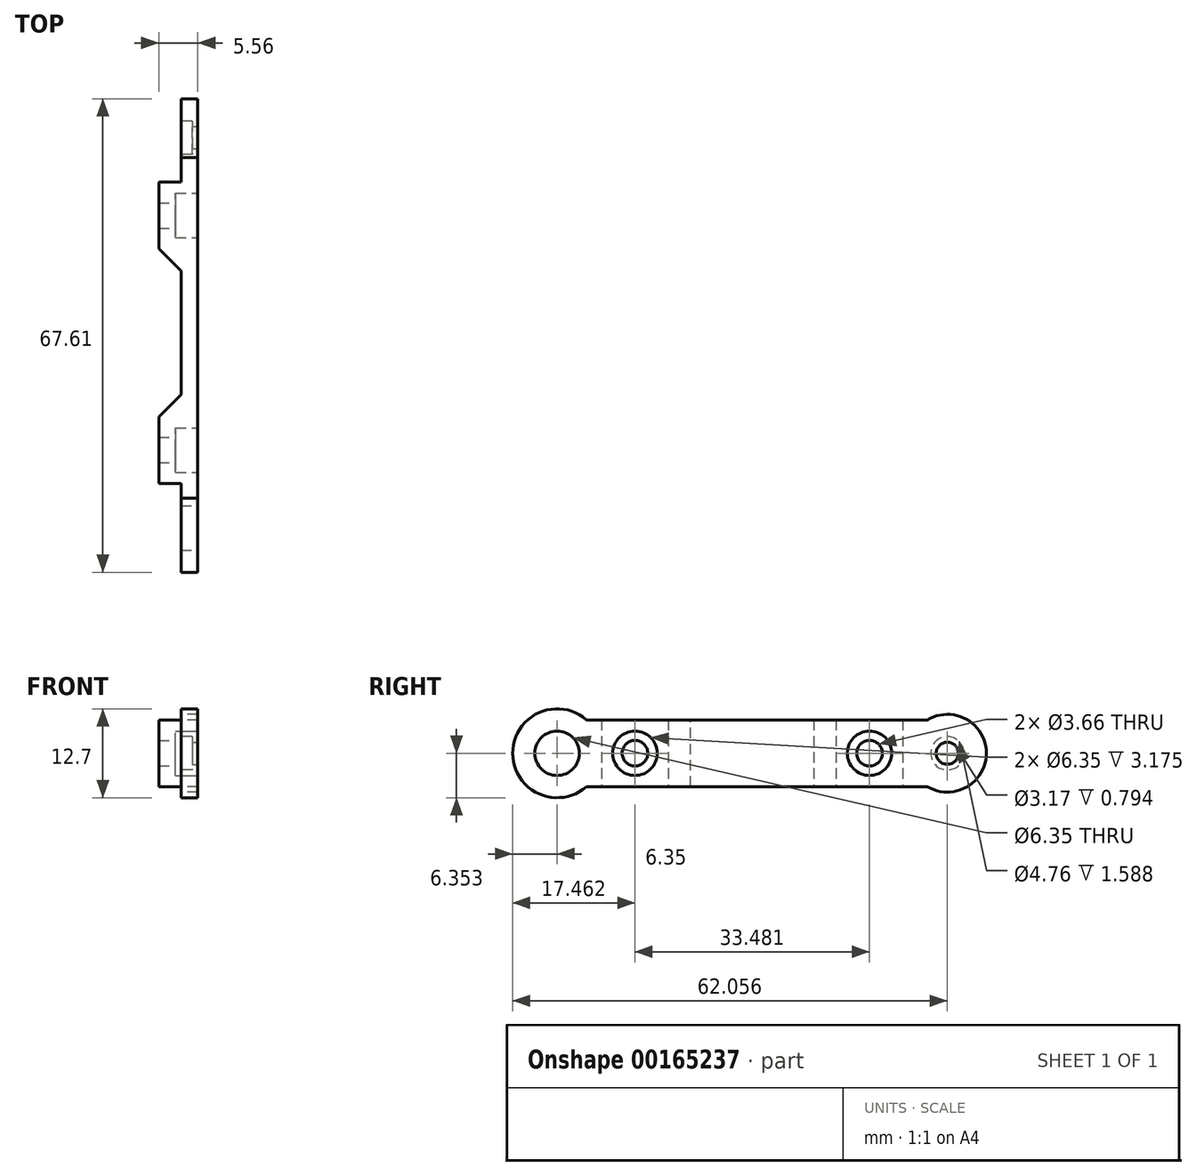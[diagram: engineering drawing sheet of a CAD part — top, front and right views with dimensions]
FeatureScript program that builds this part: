
annotation { "Feature Type Name" : "Feature", "Feature Type Description" : "" }
export const myFeature = defineFeature(function(context is Context, id is Id, definition is map)
    precondition{}
    {
        {
            var Q0;
            Q0=qCreatedBy(makeId("Top.planeOp"),FACE);
            var sketch = newSketch(context, id + "F0", { "sketchPlane" : qUnion([Q0])});
            skLineSegment(sketch, "E0.top", {"start": v(0, 55.7) * mm, "end": v(-2.38, 55.7) * mm});
            skLineSegment(sketch, "E0.left", {"start": v(0, 0) * mm, "end": v(0, 55.7) * mm});
            skLineSegment(sketch, "E0.right", {"start": v(-2.38, 49.36) * mm, "end": v(-2.38, 55.7) * mm});
            skLineSegment(sketch, "E1", {"start": v(0, 0) * mm, "end": v(-2.38, 0) * mm});
            skLineSegment(sketch, "E2", {"start": v(-2.38, 0) * mm, "end": v(-2.38, 6.35) * mm});
            skLineSegment(sketch, "E3", {"start": v(-2.38, 6.35) * mm, "end": v(-5.56, 6.35) * mm});
            skLineSegment(sketch, "E4", {"start": v(-5.56, 6.35) * mm, "end": v(-5.56, 15.87) * mm});
            skLineSegment(sketch, "E5", {"start": v(-5.56, 15.87) * mm, "end": v(-2.38, 15.87) * mm});
            skLineSegment(sketch, "E6", {"start": v(-2.38, 15.87) * mm, "end": v(-2.38, 39.83) * mm});
            skLineSegment(sketch, "E7", {"start": v(-2.38, 39.83) * mm, "end": v(-5.56, 39.83) * mm});
            skLineSegment(sketch, "E8", {"start": v(-5.56, 39.83) * mm, "end": v(-5.56, 49.36) * mm});
            skLineSegment(sketch, "E9", {"start": v(-5.56, 49.36) * mm, "end": v(-2.38, 49.36) * mm});
            skLineSegment(sketch, "E10", {"start": v(-2.38, 27.85) * mm, "end": v(0, 27.85) * mm, "construction": true});
            skSolve(sketch);
        }
        {
            var Q0;
            Q0 = qSketchRegion(id + "F0", true);
            extrude(context, id + "F1", {"entities" : qUnion([Q0]), "depth" : 9.52 * mm});
        }
        {
            var Q0;
            Q0=makeQuery(id+"F1.opExtrude","SWEPT_FACE",FACE,{"disambiguationData":[OSD([sQuery(id+"F0.wireOp",EDGE,"E0.right")])]});
            var sketch = newSketch(context, id + "F2", { "sketchPlane" : qUnion([Q0])});
            skCircle(sketch, "E11", {"center": v(-55.7, 4.76) * mm, "radius": 5.56 * mm});
            skCircle(sketch, "E12", {"center": v(0, 4.76) * mm, "radius": 6.35 * mm});
            skSolve(sketch);
        }
        {
            var Q0;
            Q0 = qSketchRegion(id + "F2", true);
            var Q1;
            Q1=makeQuery(id+"F1.opExtrude","SWEPT_FACE",FACE,{"disambiguationData":[OSD([sQuery(id+"F0.wireOp",EDGE,"E0.left")])]});
            extrude(context, id + "F3", {"entities" : qUnion([Q0]), "operationType" : NewBodyOperationType.ADD, "endBound" : BoundingType.UP_TO_SURFACE, "oppositeDirection" : true, "endBoundEntityFace" : qUnion([Q1]), "depth" : 25.4 * mm});
        }
        {
            var Q0;
            Q0=makeQuery(id+"F3.boolean.opBoolean","MERGE",FACE,{"derivedFrom":[makeQuery(id+"F1.opExtrude","SWEPT_FACE",FACE,{"disambiguationData":[OSD([sQuery(id+"F0.wireOp",EDGE,"E0.left")])]}),makeQuery(id+"F3.opExtrude","CAP_FACE",FACE,{"disambiguationData":[OSD([sQuery(id+"F2.wireOp",EDGE,"E11")])],"isStart":false}),makeQuery(id+"F3.opExtrude","CAP_FACE",FACE,{"disambiguationData":[OSD([sQuery(id+"F2.wireOp",EDGE,"E12")])],"isStart":false})]});
            var sketch = newSketch(context, id + "F4", { "sketchPlane" : qUnion([Q0])});
            skCircle(sketch, "E13", {"center": v(0, 4.76) * mm, "radius": 3.18 * mm});
            skLineSegment(sketch, "E14", {"start": v(11.11, 9.52) * mm, "end": v(11.11, 0) * mm, "construction": true});
            skLineSegment(sketch, "E15", {"start": v(44.6, 9.53) * mm, "end": v(44.6, 0) * mm, "construction": true});
            skCircle(sketch, "E16", {"center": v(11.11, 4.76) * mm, "radius": 1.83 * mm});
            skCircle(sketch, "E17", {"center": v(44.6, 4.76) * mm, "radius": 1.83 * mm});
            skCircle(sketch, "E18", {"center": v(55.7, 4.76) * mm, "radius": 1.59 * mm});
            skSolve(sketch);
        }
        {
            var Q0;
            Q0 = qSketchRegion(id + "F4", true);
            var Q1;
            Q1=makeQuery(id+"F1.opExtrude","SWEPT_FACE",FACE,{"disambiguationData":[OSD([sQuery(id+"F0.wireOp",EDGE,"E4")])]});
            extrude(context, id + "F5", {"entities" : qUnion([Q0]), "operationType" : NewBodyOperationType.REMOVE, "endBound" : BoundingType.UP_TO_SURFACE, "oppositeDirection" : true, "endBoundEntityFace" : qUnion([Q1]), "depth" : 25.4 * mm});
        }
        {
            var Q0;
            Q0=makeQuery(id+"F3.boolean.opBoolean","MERGE",FACE,{"derivedFrom":[makeQuery(id+"F1.opExtrude","SWEPT_FACE",FACE,{"disambiguationData":[OSD([sQuery(id+"F0.wireOp",EDGE,"E0.right")])]}),makeQuery(id+"F3.opExtrude","CAP_FACE",FACE,{"disambiguationData":[OSD([sQuery(id+"F2.wireOp",EDGE,"E11")])],"isStart":true})]});
            var sketch = newSketch(context, id + "F6", { "sketchPlane" : qUnion([Q0])});
            skCircle(sketch, "E19", {"center": v(-55.7, 4.76) * mm, "radius": 2.38 * mm});
            skSolve(sketch);
        }
        {
            var Q0;
            Q0 = qSketchRegion(id + "F6", true);
            extrude(context, id + "F7", {"entities" : qUnion([Q0]), "operationType" : NewBodyOperationType.REMOVE, "oppositeDirection" : true, "depth" : 1.59 * mm});
        }
        {
            var Q0;
            Q0=makeQuery(id+"F1.opExtrude","SWEPT_EDGE",EDGE,{"disambiguationData":[OSD([sQuery(id+"F0.wireOp",EDGE,"E6"),sQuery(id+"F0.wireOp",EDGE,"E7")])]});
            var Q1;
            Q1=makeQuery(id+"F1.opExtrude","SWEPT_EDGE",EDGE,{"disambiguationData":[OSD([sQuery(id+"F0.wireOp",EDGE,"E5"),sQuery(id+"F0.wireOp",EDGE,"E6")])]});
            chamfer(context, id + "F8", {"entities" : qUnion([Q0, Q1]), "width" : 3.17 * mm, "tangentPropagation" : true});
        }
        {
            var Q0;
            Q0=makeQuery(id+"F3.boolean.opBoolean","MERGE",FACE,{"derivedFrom":[makeQuery(id+"F1.opExtrude","SWEPT_FACE",FACE,{"disambiguationData":[OSD([sQuery(id+"F0.wireOp",EDGE,"E0.left")])]}),makeQuery(id+"F3.opExtrude","CAP_FACE",FACE,{"disambiguationData":[OSD([sQuery(id+"F2.wireOp",EDGE,"E11")])],"isStart":false}),makeQuery(id+"F3.opExtrude","CAP_FACE",FACE,{"disambiguationData":[OSD([sQuery(id+"F2.wireOp",EDGE,"E12")])],"isStart":false})]});
            var sketch = newSketch(context, id + "F9", { "sketchPlane" : qUnion([Q0])});
            skCircle(sketch, "E20", {"center": v(11.11, 4.76) * mm, "radius": 3.18 * mm});
            skCircle(sketch, "E21", {"center": v(44.6, 4.76) * mm, "radius": 3.18 * mm});
            skSolve(sketch);
        }
        {
            var Q0;
            Q0 = qSketchRegion(id + "F9", true);
            extrude(context, id + "F10", {"entities" : qUnion([Q0]), "operationType" : NewBodyOperationType.REMOVE, "oppositeDirection" : true, "depth" : 3.17 * mm});
        }
    });
